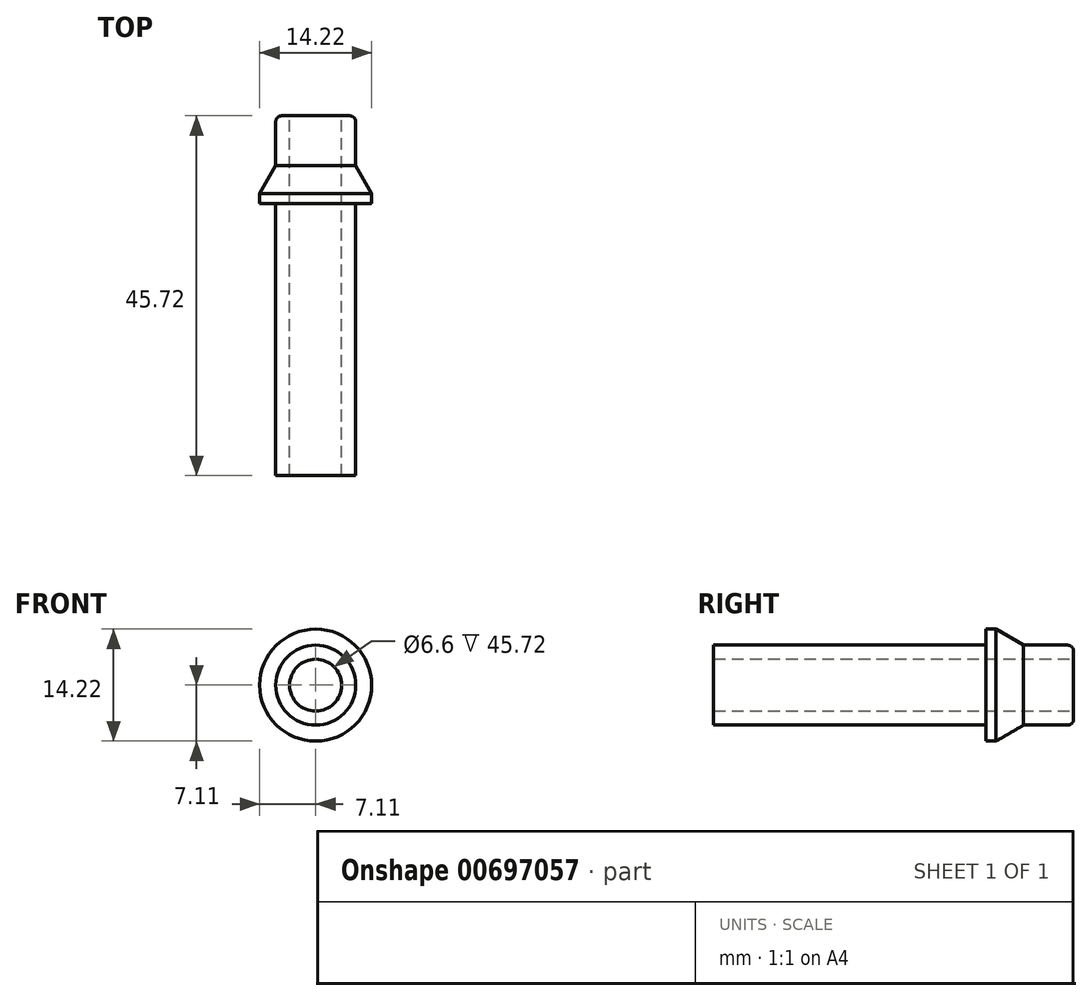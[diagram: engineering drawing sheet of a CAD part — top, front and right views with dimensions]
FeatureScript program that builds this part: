
annotation { "Feature Type Name" : "Feature", "Feature Type Description" : "" }
export const myFeature = defineFeature(function(context is Context, id is Id, definition is map)
    precondition{}
    {
        {
            var Q0;
            Q0=qCreatedBy(makeId("Front.planeOp"),FACE);
            var sketch = newSketch(context, id + "F0", { "sketchPlane" : qUnion([Q0])});
            skCircle(sketch, "E0", {"center": v(0, 0) * mm, "radius": 3.3 * mm});
            skCircle(sketch, "E1", {"center": v(0, 0) * mm, "radius": 5.08 * mm});
            skSolve(sketch);
        }
        {
            var Q0;
            Q0 = qSketchRegion(id + "F0", true);
            extrude(context, id + "F1", {"entities" : qUnion([Q0]), "depth" : 45.72 * mm, "offsetDistance" : 25.4 * mm});
        }
        {
            var Q0;
            Q0=qCreatedBy(makeId("Right.planeOp"),FACE);
            var sketch = newSketch(context, id + "F2", { "sketchPlane" : qUnion([Q0])});
            skLineSegment(sketch, "E2", {"start": v(-38.1, 5.08) * mm, "end": v(0, 5.08) * mm});
            skLineSegment(sketch, "E3.bottom", {"start": v(-6.35, 5.08) * mm, "end": v(-11.14, 5.08) * mm});
            skLineSegment(sketch, "E3.right", {"start": v(-11.14, 5.08) * mm, "end": v(-11.14, 7.11) * mm});
            skLineSegment(sketch, "E4", {"start": v(-11.14, 7.11) * mm, "end": v(-9.87, 7.11) * mm});
            skLineSegment(sketch, "E5", {"start": v(-9.87, 7.11) * mm, "end": v(-6.35, 5.08) * mm});
            skSolve(sketch);
        }
        {
            var Q0;
            Q0 = qSketchRegion(id + "F2", true);
            var Q1;
            Q1=makeQuery(id+"F1.opExtrude","CAP_EDGE",EDGE,{"disambiguationData":[OSD([sQuery(id+"F0.wireOp",EDGE,"E0")])],"isStart":false});
            revolve(context, id + "F3", {"operationType" : NewBodyOperationType.ADD, "entities" : qUnion([Q0]), "axis" : qUnion([Q1]), "revolveType" : RevolveType.FULL});
        }
        {
            var Q0;
            Q0=makeQuery(id+"F1.opExtrude","CAP_EDGE",EDGE,{"disambiguationData":[OSD([sQuery(id+"F0.wireOp",EDGE,"E1")])],"isStart":true});
            fillet(context, id + "F4", {"entities" : qUnion([Q0]), "radius" : 0.76 * mm, "tangentPropagation" : true, "allowEdgeOverflow" : false});
        }
    });
